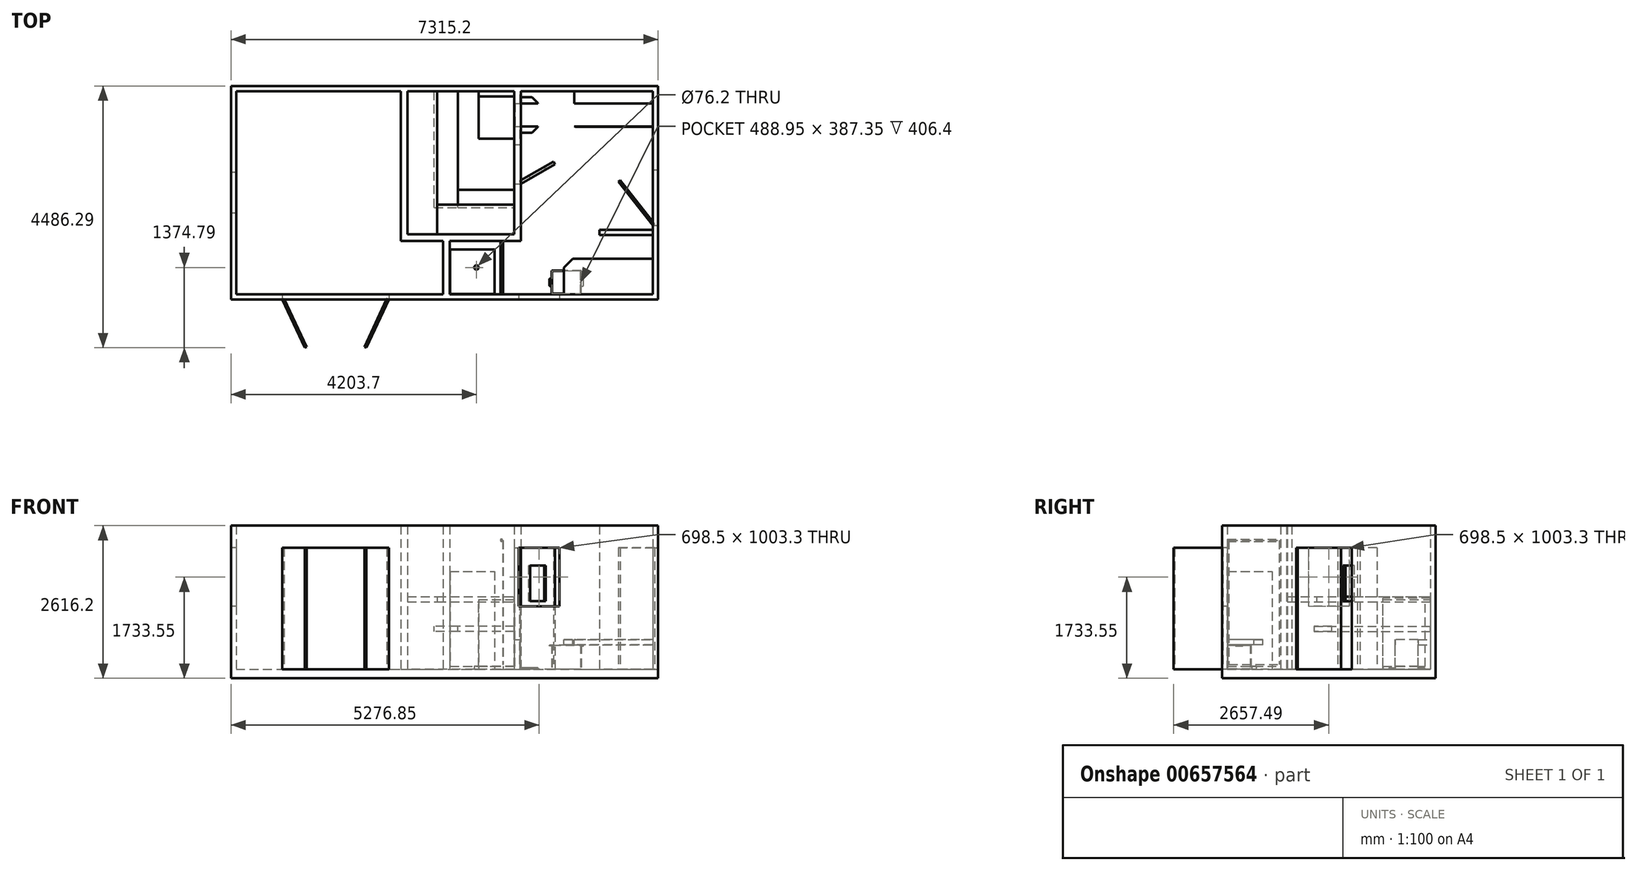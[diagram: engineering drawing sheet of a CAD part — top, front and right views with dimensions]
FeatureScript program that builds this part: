
annotation { "Feature Type Name" : "Feature", "Feature Type Description" : "" }
export const myFeature = defineFeature(function(context is Context, id is Id, definition is map)
    precondition{}
    {
        {
            var Q0;
            Q0=qCreatedBy(makeId("Top.planeOp"),FACE);
            var sketch = newSketch(context, id + "F0", { "sketchPlane" : qUnion([Q0])});
            skLineSegment(sketch, "E0.bottom", {"start": v(-3657.6, -1828.8) * mm, "end": v(3657.6, -1828.8) * mm});
            skLineSegment(sketch, "E0.top", {"start": v(-3657.6, 1828.8) * mm, "end": v(3657.6, 1828.8) * mm});
            skLineSegment(sketch, "E0.left", {"start": v(-3657.6, -1828.8) * mm, "end": v(-3657.6, 1828.8) * mm});
            skLineSegment(sketch, "E0.right", {"start": v(3657.6, -1828.8) * mm, "end": v(3657.6, 1828.8) * mm});
            skPoint(sketch, "E0.middle", {"position": v(0, 0) * mm});
            skSolve(sketch);
        }
        {
            var Q0;
            Q0=makeQuery(id+"F0.imprint","IMPRINT",FACE,{"disambiguationData":[TD([[makeQuery(id+"F0.imprint","IMPRINT",EDGE,{"derivedFrom":sQuery(id+"F0.wireOp",EDGE,"E0.bottom")}),1.0]])]});
            extrude(context, id + "F1", {"entities" : qUnion([Q0]), "depth" : 152.4 * mm});
        }
        {
            var Q0;
            Q0=makeQuery(id+"F1.opExtrude","CAP_FACE",FACE,{"disambiguationData":[OSD([sQuery(id+"F0.wireOp",EDGE,"E0.bottom"),sQuery(id+"F0.wireOp",EDGE,"E0.top"),sQuery(id+"F0.wireOp",EDGE,"E0.left"),sQuery(id+"F0.wireOp",EDGE,"E0.right")])],"isStart":false});
            var sketch = newSketch(context, id + "F2", { "sketchPlane" : qUnion([Q0])});
            skLineSegment(sketch, "E1.0", {"start": v(-3657.6, -1828.8) * mm, "end": v(-3657.6, 1828.8) * mm});
            skLineSegment(sketch, "E1.1", {"start": v(-3657.6, 1828.8) * mm, "end": v(3657.6, 1828.8) * mm});
            skLineSegment(sketch, "E1.2", {"start": v(3657.6, -1828.8) * mm, "end": v(3657.6, 1828.8) * mm});
            skLineSegment(sketch, "E1.3", {"start": v(-3657.6, -1828.8) * mm, "end": v(3657.6, -1828.8) * mm});
            skLineSegment(sketch, "E2.bottom", {"start": v(-3568.7, 1739.9) * mm, "end": v(3568.7, 1739.9) * mm});
            skLineSegment(sketch, "E2.top", {"start": v(-3568.7, -1739.9) * mm, "end": v(3568.7, -1739.9) * mm});
            skLineSegment(sketch, "E2.left", {"start": v(-3568.7, 1739.9) * mm, "end": v(-3568.7, -1739.9) * mm});
            skLineSegment(sketch, "E2.right", {"start": v(3568.7, 1739.9) * mm, "end": v(3568.7, -1739.9) * mm});
            skLineSegment(sketch, "E3", {"start": v(3568.7, 0) * mm, "end": v(0, 0) * mm, "construction": true});
            skSolve(sketch);
        }
        {
            var Q0;
            Q0=qSketchRegion(id+"F2",true);
            extrude(context, id + "F3", {"entities" : qUnion([Q0]), "depth" : 2463.8 * mm});
        }
        {
            var Q0;
            Q0=makeQuery(id+"F3.opExtrude","SWEPT_FACE",FACE,{"disambiguationData":[OSD([sQuery(id+"F2.wireOp",EDGE,"E1.2")])]});
            var sketch = newSketch(context, id + "F4", { "sketchPlane" : qUnion([Q0])});
            skLineSegment(sketch, "E4.bottom", {"start": v(-558.8, 152.4) * mm, "end": v(393.7, 152.4) * mm});
            skLineSegment(sketch, "E4.top", {"start": v(-558.8, 2235.2) * mm, "end": v(393.7, 2235.2) * mm});
            skLineSegment(sketch, "E4.left", {"start": v(-558.8, 152.4) * mm, "end": v(-558.8, 2235.2) * mm});
            skLineSegment(sketch, "E4.right", {"start": v(393.7, 152.4) * mm, "end": v(393.7, 2235.2) * mm});
            skSolve(sketch);
        }
        {
            var Q0;
            Q0=qSketchRegion(id+"F4",true);
            extrude(context, id + "F5", {"entities" : qUnion([Q0]), "operationType" : NewBodyOperationType.REMOVE, "endBound" : BoundingType.UP_TO_NEXT, "oppositeDirection" : true, "depth" : 25.4 * mm});
        }
        {
            var Q0;
            Q0=makeQuery(id+"F3.opExtrude","SWEPT_FACE",FACE,{"disambiguationData":[OSD([sQuery(id+"F2.wireOp",EDGE,"E1.3")])]});
            var sketch = newSketch(context, id + "F6", { "sketchPlane" : qUnion([Q0])});
            skLineSegment(sketch, "E5.bottom", {"start": v(-2781.3, 152.4) * mm, "end": v(-952.5, 152.4) * mm});
            skLineSegment(sketch, "E5.top", {"start": v(-2781.3, 2235.2) * mm, "end": v(-952.5, 2235.2) * mm});
            skLineSegment(sketch, "E5.left", {"start": v(-2781.3, 152.4) * mm, "end": v(-2781.3, 2235.2) * mm});
            skLineSegment(sketch, "E5.right", {"start": v(-952.5, 152.4) * mm, "end": v(-952.5, 2235.2) * mm});
            skLineSegment(sketch, "E6.bottom", {"start": v(1270, 2235.2) * mm, "end": v(1968.5, 2235.2) * mm});
            skLineSegment(sketch, "E6.top", {"start": v(1270, 1231.9) * mm, "end": v(1968.5, 1231.9) * mm});
            skLineSegment(sketch, "E6.left", {"start": v(1270, 2235.2) * mm, "end": v(1270, 1231.9) * mm});
            skLineSegment(sketch, "E6.right", {"start": v(1968.5, 2235.2) * mm, "end": v(1968.5, 1231.9) * mm});
            skSolve(sketch);
        }
        {
            var Q0;
            Q0=qSketchRegion(id+"F6",true);
            extrude(context, id + "F7", {"entities" : qUnion([Q0]), "operationType" : NewBodyOperationType.REMOVE, "endBound" : BoundingType.UP_TO_NEXT, "oppositeDirection" : true, "depth" : 25.4 * mm});
        }
        {
            var Q0;
            Q0=makeQuery(id+"F3.opExtrude","SWEPT_FACE",FACE,{"disambiguationData":[OSD([sQuery(id+"F2.wireOp",EDGE,"E1.0")])]});
            var sketch = newSketch(context, id + "F8", { "sketchPlane" : qUnion([Q0])});
            skLineSegment(sketch, "E7.bottom", {"start": v(-349.25, 2235.2) * mm, "end": v(349.25, 2235.2) * mm});
            skLineSegment(sketch, "E7.top", {"start": v(-349.25, 1231.9) * mm, "end": v(349.25, 1231.9) * mm});
            skLineSegment(sketch, "E7.left", {"start": v(-349.25, 2235.2) * mm, "end": v(-349.25, 1231.9) * mm});
            skLineSegment(sketch, "E7.right", {"start": v(349.25, 2235.2) * mm, "end": v(349.25, 1231.9) * mm});
            skLineSegment(sketch, "E8", {"start": v(0, 2235.2) * mm, "end": v(0, 1231.9) * mm, "construction": true});
            skSolve(sketch);
        }
        {
            var Q0;
            Q0=qSketchRegion(id+"F8",true);
            extrude(context, id + "F9", {"entities" : qUnion([Q0]), "operationType" : NewBodyOperationType.REMOVE, "endBound" : BoundingType.UP_TO_NEXT, "oppositeDirection" : true, "depth" : 25.4 * mm});
        }
        {
            var Q0;
            Q0=makeQuery(id+"F1.opExtrude","CAP_FACE",FACE,{"disambiguationData":[OSD([sQuery(id+"F0.wireOp",EDGE,"E0.bottom"),sQuery(id+"F0.wireOp",EDGE,"E0.top"),sQuery(id+"F0.wireOp",EDGE,"E0.left"),sQuery(id+"F0.wireOp",EDGE,"E0.right")])],"isStart":false});
            var sketch = newSketch(context, id + "F10", { "sketchPlane" : qUnion([Q0])});
            skLineSegment(sketch, "E9.bottom", {"start": v(-25.4, -1739.9) * mm, "end": v(88.9, -1739.9) * mm});
            skLineSegment(sketch, "E9.top", {"start": v(-749.3, 1739.9) * mm, "end": v(-635, 1739.9) * mm});
            skLineSegment(sketch, "E9.left", {"start": v(-25.4, -1739.9) * mm, "end": v(-25.4, -825.5) * mm});
            skLineSegment(sketch, "E9.right", {"start": v(88.9, -1739.9) * mm, "end": v(88.9, -825.5) * mm});
            skLineSegment(sketch, "E10.top", {"start": v(1193.8, 1739.9) * mm, "end": v(1308.1, 1739.9) * mm});
            skLineSegment(sketch, "E11", {"start": v(1193.8, 1739.9) * mm, "end": v(1193.8, -711.2) * mm});
            skLineSegment(sketch, "E12", {"start": v(1193.8, -711.2) * mm, "end": v(-635, -711.2) * mm});
            skLineSegment(sketch, "E13", {"start": v(-749.3, -825.5) * mm, "end": v(1308.1, -825.5) * mm});
            skLineSegment(sketch, "E14", {"start": v(1308.1, -825.5) * mm, "end": v(1308.1, 1739.9) * mm});
            skLineSegment(sketch, "E15", {"start": v(-635, -711.2) * mm, "end": v(-635, 1739.9) * mm});
            skLineSegment(sketch, "E16", {"start": v(-749.3, -825.5) * mm, "end": v(-749.3, 1739.9) * mm});
            skLineSegment(sketch, "E17", {"start": v(-25.4, -825.5) * mm, "end": v(88.9, -825.5) * mm});
            skSolve(sketch);
        }
        {
            var Q0;
            Q0=qSketchRegion(id+"F10",true);
            var Q1;
            Q1=makeQuery(id+"F3.opExtrude","CAP_FACE",FACE,{"disambiguationData":[OSD([sQuery(id+"F2.wireOp",EDGE,"E1.0"),sQuery(id+"F2.wireOp",EDGE,"E1.1"),sQuery(id+"F2.wireOp",EDGE,"E1.2"),sQuery(id+"F2.wireOp",EDGE,"E1.3"),sQuery(id+"F2.wireOp",EDGE,"E2.bottom"),sQuery(id+"F2.wireOp",EDGE,"E2.top"),sQuery(id+"F2.wireOp",EDGE,"E2.left"),sQuery(id+"F2.wireOp",EDGE,"E2.right")])],"isStart":false});
            extrude(context, id + "F11", {"entities" : qUnion([Q0]), "endBound" : BoundingType.UP_TO_SURFACE, "endBoundEntityFace" : qUnion([Q1]), "depth" : 25.4 * mm});
        }
        {
            var Q0;
            Q0=makeQuery(id+"F1.opExtrude","CAP_FACE",FACE,{"disambiguationData":[OSD([sQuery(id+"F0.wireOp",EDGE,"E0.bottom"),sQuery(id+"F0.wireOp",EDGE,"E0.top"),sQuery(id+"F0.wireOp",EDGE,"E0.left"),sQuery(id+"F0.wireOp",EDGE,"E0.right")])],"isStart":false});
            var sketch = newSketch(context, id + "F12", { "sketchPlane" : qUnion([Q0])});
            skLineSegment(sketch, "E18.bottom", {"start": v(3568.7, -723.9) * mm, "end": v(2654.3, -723.9) * mm});
            skLineSegment(sketch, "E18.top", {"start": v(3568.7, -635) * mm, "end": v(2654.3, -635) * mm});
            skLineSegment(sketch, "E18.left", {"start": v(3568.7, -723.9) * mm, "end": v(3568.7, -635) * mm});
            skLineSegment(sketch, "E18.right", {"start": v(2654.3, -723.9) * mm, "end": v(2654.3, -635) * mm});
            skSolve(sketch);
        }
        {
            var Q0;
            Q0=qSketchRegion(id+"F12",true);
            var Q1;
            Q1=makeQuery(id+"F3.opExtrude","CAP_FACE",FACE,{"disambiguationData":[OSD([sQuery(id+"F2.wireOp",EDGE,"E1.0"),sQuery(id+"F2.wireOp",EDGE,"E1.1"),sQuery(id+"F2.wireOp",EDGE,"E1.2"),sQuery(id+"F2.wireOp",EDGE,"E1.3"),sQuery(id+"F2.wireOp",EDGE,"E2.bottom"),sQuery(id+"F2.wireOp",EDGE,"E2.top"),sQuery(id+"F2.wireOp",EDGE,"E2.left"),sQuery(id+"F2.wireOp",EDGE,"E2.right")])],"isStart":false});
            extrude(context, id + "F13", {"entities" : qUnion([Q0]), "endBound" : BoundingType.UP_TO_SURFACE, "endBoundEntityFace" : qUnion([Q1]), "depth" : 25.4 * mm});
        }
        {
            var Q0;
            Q0=makeQuery(id+"F11.opExtrude","SWEPT_FACE",FACE,{"disambiguationData":[OSD([sQuery(id+"F10.wireOp",EDGE,"E14")])]});
            var sketch = newSketch(context, id + "F14", { "sketchPlane" : qUnion([Q0])});
            skLineSegment(sketch, "E19.bottom", {"start": v(152.4, 152.4) * mm, "end": v(825.5, 152.4) * mm});
            skLineSegment(sketch, "E19.top", {"start": v(152.4, 2235.2) * mm, "end": v(825.5, 2235.2) * mm});
            skLineSegment(sketch, "E19.left", {"start": v(152.4, 152.4) * mm, "end": v(152.4, 2235.2) * mm});
            skLineSegment(sketch, "E19.right", {"start": v(825.5, 152.4) * mm, "end": v(825.5, 2235.2) * mm});
            skSolve(sketch);
        }
        {
            var Q0;
            Q0=qSketchRegion(id+"F14",true);
            extrude(context, id + "F15", {"entities" : qUnion([Q0]), "operationType" : NewBodyOperationType.REMOVE, "endBound" : BoundingType.UP_TO_NEXT, "oppositeDirection" : true, "depth" : 25.4 * mm});
        }
        {
            var Q0;
            Q0=qCreatedBy(makeId("Front.planeOp"),FACE);
            var sketch = newSketch(context, id + "F16", { "sketchPlane" : qUnion([Q0])});
            skLineSegment(sketch, "E20.bottom", {"start": v(88.9, 152.4) * mm, "end": v(127, 152.4) * mm});
            skLineSegment(sketch, "E20.top", {"start": v(88.9, 1397) * mm, "end": v(127, 1397) * mm});
            skLineSegment(sketch, "E20.left", {"start": v(88.9, 152.4) * mm, "end": v(88.9, 1397) * mm});
            skLineSegment(sketch, "E20.right", {"start": v(127, 152.4) * mm, "end": v(127, 1397) * mm});
            skSolve(sketch);
        }
        {
            var Q0;
            Q0=qSketchRegion(id+"F16",true);
            extrude(context, id + "F17", {"entities" : qUnion([Q0]), "endBound" : BoundingType.SYMMETRIC, "depth" : 88.9 * mm});
        }
        {
            var Q0;
            Q0=makeQuery(id+"F17.opExtrude","SWEPT_BODY",BODY,{"disambiguationData":[OSD([sQuery(id+"F16.wireOp",EDGE,"E20.bottom"),sQuery(id+"F16.wireOp",EDGE,"E20.top"),sQuery(id+"F16.wireOp",EDGE,"E20.left"),sQuery(id+"F16.wireOp",EDGE,"E20.right")])]});
            deleteBodies(context, id + "F18", {"entities" : qUnion([Q0])});
        }
        {
            var Q0;
            Q0=qCreatedBy(makeId("Front.planeOp"),FACE);
            var sketch = newSketch(context, id + "F19", { "sketchPlane" : qUnion([Q0])});
            skLineSegment(sketch, "E21.bottom", {"start": v(-635, 1397) * mm, "end": v(-127, 1397) * mm});
            skLineSegment(sketch, "E21.top", {"start": v(-635, 1308.1) * mm, "end": v(-127, 1308.1) * mm});
            skLineSegment(sketch, "E21.left", {"start": v(-635, 1397) * mm, "end": v(-635, 1308.1) * mm});
            skLineSegment(sketch, "E21.right", {"start": v(-127, 1397) * mm, "end": v(-127, 1308.1) * mm});
            skSolve(sketch);
        }
        {
            var Q0;
            Q0=qSketchRegion(id+"F19",true);
            extrude(context, id + "F20", {"entities" : qUnion([Q0]), "endBound" : BoundingType.UP_TO_NEXT, "depth" : 812.8 * mm, "hasSecondDirection" : true, "secondDirectionBound" : SecondDirectionBoundingType.UP_TO_NEXT, "secondDirectionOppositeDirection" : true, "secondDirectionDepth" : 25.4 * mm, "offsetDistance" : 25.4 * mm});
        }
        {
            var Q0;
            Q0=makeQuery(id+"F20.opExtrude","SWEPT_FACE",FACE,{"disambiguationData":[OSD([sQuery(id+"F19.wireOp",EDGE,"E21.bottom")])]});
            var sketch = newSketch(context, id + "F21", { "sketchPlane" : qUnion([Q0])});
            skLineSegment(sketch, "E22.top", {"start": v(-127, -711.2) * mm, "end": v(1193.8, -711.2) * mm});
            skLineSegment(sketch, "E22.left", {"start": v(-127, -711.2) * mm, "end": v(-127, -203.2) * mm});
            skLineSegment(sketch, "E22.right", {"start": v(1193.8, -711.2) * mm, "end": v(1193.8, -203.2) * mm});
            skLineSegment(sketch, "E23", {"start": v(1193.8, -203.2) * mm, "end": v(-127, -203.2) * mm});
            skSolve(sketch);
        }
        {
            var Q0;
            Q0=qSketchRegion(id+"F21",true);
            var Q1;
            Q1=makeQuery(id+"F20.opExtrude","CAP_VERTEX",VERTEX,{"disambiguationData":[OSD([sQuery(id+"F2.wireOp",EDGE,"E2.top"),sQuery(id+"F19.wireOp",EDGE,"E21.top"),sQuery(id+"F19.wireOp",EDGE,"E21.right")])],"isStart":false});
            extrude(context, id + "F22", {"entities" : qUnion([Q0]), "endBound" : BoundingType.UP_TO_VERTEX, "oppositeDirection" : true, "endBoundEntityVertex" : qUnion([Q1]), "depth" : 25.4 * mm});
        }
        {
            var Q0;
            Q0=qCreatedBy(makeId("Front.planeOp"),FACE);
            var sketch = newSketch(context, id + "F23", { "sketchPlane" : qUnion([Q0])});
            skLineSegment(sketch, "E24.bottom", {"start": v(-177.8, 889) * mm, "end": v(228.6, 889) * mm});
            skLineSegment(sketch, "E24.top", {"start": v(-177.8, 800.1) * mm, "end": v(228.6, 800.1) * mm});
            skLineSegment(sketch, "E24.left", {"start": v(-177.8, 889) * mm, "end": v(-177.8, 800.1) * mm});
            skLineSegment(sketch, "E24.right", {"start": v(228.6, 889) * mm, "end": v(228.6, 800.1) * mm});
            skSolve(sketch);
        }
        {
            var Q0;
            Q0=qSketchRegion(id+"F23",true);
            extrude(context, id + "F24", {"entities" : qUnion([Q0]), "depth" : 254 * mm, "hasSecondDirection" : true, "secondDirectionBound" : SecondDirectionBoundingType.UP_TO_NEXT, "secondDirectionOppositeDirection" : true, "secondDirectionDepth" : 1282.7 * mm, "offsetDistance" : 25.4 * mm});
        }
        {
            var Q0;
            Q0=makeQuery(id+"F24.opExtrude","SWEPT_FACE",FACE,{"disambiguationData":[OSD([sQuery(id+"F23.wireOp",EDGE,"E24.bottom")])]});
            var sketch = newSketch(context, id + "F25", { "sketchPlane" : qUnion([Q0])});
            skLineSegment(sketch, "E25.bottom", {"start": v(1193.8, 50.8) * mm, "end": v(228.6, 50.8) * mm});
            skLineSegment(sketch, "E25.top", {"start": v(228.6, -254) * mm, "end": v(1193.8, -254) * mm});
            skLineSegment(sketch, "E25.left", {"start": v(228.6, 50.8) * mm, "end": v(228.6, -254) * mm});
            skLineSegment(sketch, "E25.right", {"start": v(1193.8, 50.8) * mm, "end": v(1193.8, -254) * mm});
            skSolve(sketch);
        }
        {
            var Q0;
            Q0=makeQuery(id+"F3.opExtrude","SWEPT_FACE",FACE,{"disambiguationData":[OSD([sQuery(id+"F2.wireOp",EDGE,"E2.bottom")])]});
            var sketch = newSketch(context, id + "F26", { "sketchPlane" : qUnion([Q0])});
            skLineSegment(sketch, "E26.bottom", {"start": v(3568.7, 660.4) * mm, "end": v(2222.5, 660.4) * mm});
            skLineSegment(sketch, "E26.top", {"start": v(2222.5, 571.5) * mm, "end": v(3568.7, 571.5) * mm});
            skLineSegment(sketch, "E26.left", {"start": v(3568.7, 660.4) * mm, "end": v(3568.7, 571.5) * mm});
            skLineSegment(sketch, "E26.right", {"start": v(2222.5, 660.4) * mm, "end": v(2222.5, 571.5) * mm});
            skSolve(sketch);
        }
        {
            var Q0;
            Q0=qSketchRegion(id+"F26",true);
            extrude(context, id + "F27", {"entities" : qUnion([Q0]), "depth" : 609.6 * mm});
        }
        {
            var Q0;
            Q0=makeQuery(id+"F27.opExtrude","SWEPT_FACE",FACE,{"disambiguationData":[OSD([sQuery(id+"F26.wireOp",EDGE,"E26.bottom")])]});
            var sketch = newSketch(context, id + "F28", { "sketchPlane" : qUnion([Q0])});
            skLineSegment(sketch, "E27.bottom", {"start": v(2222.5, 1130.3) * mm, "end": v(2628.9, 1130.3) * mm});
            skLineSegment(sketch, "E27.top", {"start": v(2222.5, 114.3) * mm, "end": v(2628.9, 114.3) * mm});
            skLineSegment(sketch, "E27.left", {"start": v(2222.5, 114.3) * mm, "end": v(2222.5, 1130.3) * mm});
            skLineSegment(sketch, "E27.right", {"start": v(2628.9, 114.3) * mm, "end": v(2628.9, 1130.3) * mm});
            skSolve(sketch);
        }
        {
            var Q0;
            Q0=qSketchRegion(id+"F25",true);
            var Q1;
            Q1=makeQuery(id+"F24.opExtrude","CAP_VERTEX",VERTEX,{"disambiguationData":[OSD([sQuery(id+"F23.wireOp",EDGE,"E24.top"),sQuery(id+"F23.wireOp",EDGE,"E24.right")])],"isStart":true});
            extrude(context, id + "F29", {"entities" : qUnion([Q0]), "endBound" : BoundingType.UP_TO_VERTEX, "oppositeDirection" : true, "endBoundEntityVertex" : qUnion([Q1]), "depth" : 25.4 * mm});
        }
        {
            var Q0;
            Q0=makeQuery(id+"F1.opExtrude","CAP_FACE",FACE,{"disambiguationData":[OSD([sQuery(id+"F0.wireOp",EDGE,"E0.bottom"),sQuery(id+"F0.wireOp",EDGE,"E0.top"),sQuery(id+"F0.wireOp",EDGE,"E0.left"),sQuery(id+"F0.wireOp",EDGE,"E0.right")])],"isStart":false});
            var sketch = newSketch(context, id + "F30", { "sketchPlane" : qUnion([Q0])});
            skLineSegment(sketch, "E28", {"start": v(1282.7, 196.4) * mm, "end": v(1308.1, 152.4) * mm});
            skLineSegment(sketch, "E29", {"start": v(1308.1, 152.4) * mm, "end": v(1891.02, 488.95) * mm});
            skLineSegment(sketch, "E30", {"start": v(1891.02, 488.95) * mm, "end": v(1865.62, 532.94) * mm});
            skLineSegment(sketch, "E31", {"start": v(1865.62, 532.94) * mm, "end": v(1282.7, 196.4) * mm});
            skSolve(sketch);
        }
        {
            var Q0;
            Q0=qSketchRegion(id+"F30",true);
            extrude(context, id + "F31", {"entities" : qUnion([Q0]), "depth" : 2082.8 * mm});
        }
        {
            var Q0;
            Q0=makeQuery(id+"F1.opExtrude","CAP_FACE",FACE,{"disambiguationData":[OSD([sQuery(id+"F0.wireOp",EDGE,"E0.bottom"),sQuery(id+"F0.wireOp",EDGE,"E0.top"),sQuery(id+"F0.wireOp",EDGE,"E0.left"),sQuery(id+"F0.wireOp",EDGE,"E0.right")])],"isStart":false});
            var sketch = newSketch(context, id + "F32", { "sketchPlane" : qUnion([Q0])});
            skLineSegment(sketch, "E32", {"start": v(3568.7, -558.8) * mm, "end": v(3598.59, -535.17) * mm});
            skLineSegment(sketch, "E33", {"start": v(3598.59, -535.17) * mm, "end": v(3007.81, 211.99) * mm});
            skLineSegment(sketch, "E34", {"start": v(3007.81, 211.99) * mm, "end": v(2977.93, 188.36) * mm});
            skLineSegment(sketch, "E35", {"start": v(2977.93, 188.36) * mm, "end": v(3568.7, -558.8) * mm});
            skSolve(sketch);
        }
        {
            var Q0;
            Q0=qSketchRegion(id+"F32",true);
            extrude(context, id + "F33", {"entities" : qUnion([Q0]), "depth" : 2082.8 * mm});
        }
        {
            var Q0;
            Q0=makeQuery(id+"F1.opExtrude","CAP_FACE",FACE,{"disambiguationData":[OSD([sQuery(id+"F0.wireOp",EDGE,"E0.bottom"),sQuery(id+"F0.wireOp",EDGE,"E0.top"),sQuery(id+"F0.wireOp",EDGE,"E0.left"),sQuery(id+"F0.wireOp",EDGE,"E0.right")])],"isStart":false});
            var sketch = newSketch(context, id + "F34", { "sketchPlane" : qUnion([Q0])});
            skLineSegment(sketch, "E36", {"start": v(88.9, -1739.9) * mm, "end": v(88.9, -971.55) * mm});
            skLineSegment(sketch, "E37", {"start": v(88.9, -1739.9) * mm, "end": v(857.25, -1739.9) * mm});
            skLineSegment(sketch, "E38.0", {"start": v(95.25, -1733.55) * mm, "end": v(857.25, -1733.55) * mm});
            skLineSegment(sketch, "E38.1", {"start": v(95.25, -1733.55) * mm, "end": v(95.25, -971.55) * mm});
            skLineSegment(sketch, "E39", {"start": v(88.9, -971.55) * mm, "end": v(95.25, -971.55) * mm});
            skLineSegment(sketch, "E40", {"start": v(857.25, -1739.9) * mm, "end": v(857.25, -1733.55) * mm});
            skSolve(sketch);
        }
        {
            var Q0;
            Q0=qSketchRegion(id+"F34",true);
            extrude(context, id + "F35", {"entities" : qUnion([Q0]), "depth" : 1676.4 * mm});
        }
        {
            var Q0;
            Q0=makeQuery(id+"F1.opExtrude","CAP_FACE",FACE,{"disambiguationData":[OSD([sQuery(id+"F0.wireOp",EDGE,"E0.bottom"),sQuery(id+"F0.wireOp",EDGE,"E0.top"),sQuery(id+"F0.wireOp",EDGE,"E0.left"),sQuery(id+"F0.wireOp",EDGE,"E0.right")])],"isStart":false});
            var sketch = newSketch(context, id + "F36", { "sketchPlane" : qUnion([Q0])});
            skLineSegment(sketch, "E41.bottom", {"start": v(88.9, -1739.9) * mm, "end": v(857.25, -1739.9) * mm});
            skLineSegment(sketch, "E41.top", {"start": v(88.9, -971.55) * mm, "end": v(857.25, -971.55) * mm});
            skLineSegment(sketch, "E41.left", {"start": v(88.9, -1739.9) * mm, "end": v(88.9, -971.55) * mm});
            skLineSegment(sketch, "E41.right", {"start": v(857.25, -1739.9) * mm, "end": v(857.25, -971.55) * mm});
            skSolve(sketch);
        }
        {
            var Q0;
            Q0=qSketchRegion(id+"F36",true);
            extrude(context, id + "F37", {"entities" : qUnion([Q0]), "operationType" : NewBodyOperationType.ADD, "depth" : 50.8 * mm});
        }
        {
            var Q0;
            Q0=makeQuery(id+"F1.opExtrude","CAP_FACE",FACE,{"disambiguationData":[OSD([sQuery(id+"F0.wireOp",EDGE,"E0.bottom"),sQuery(id+"F0.wireOp",EDGE,"E0.top"),sQuery(id+"F0.wireOp",EDGE,"E0.left"),sQuery(id+"F0.wireOp",EDGE,"E0.right")])],"isStart":false});
            var sketch = newSketch(context, id + "F38", { "sketchPlane" : qUnion([Q0])});
            skLineSegment(sketch, "E42.bottom", {"start": v(88.9, -1739.9) * mm, "end": v(1003.3, -1739.9) * mm});
            skLineSegment(sketch, "E42.top", {"start": v(88.9, -825.5) * mm, "end": v(1003.3, -825.5) * mm});
            skLineSegment(sketch, "E42.left", {"start": v(88.9, -1739.9) * mm, "end": v(88.9, -825.5) * mm});
            skLineSegment(sketch, "E42.right", {"start": v(1003.3, -1739.9) * mm, "end": v(1003.3, -825.5) * mm});
            skCircle(sketch, "E43", {"center": v(546.1, -1282.7) * mm, "radius": 38.1 * mm});
            skLineSegment(sketch, "E44", {"start": v(546.1, -825.5) * mm, "end": v(546.1, -1739.9) * mm, "construction": true});
            skSolve(sketch);
        }
        {
            var Q0;
            Q0=qSketchRegion(id+"F38",true);
            extrude(context, id + "F39", {"entities" : qUnion([Q0]), "depth" : 50.8 * mm});
        }
        {
            var Q0;
            Q0=makeQuery(id+"F3.opExtrude","SWEPT_FACE",FACE,{"disambiguationData":[OSD([sQuery(id+"F2.wireOp",EDGE,"E2.top")])]});
            var sketch = newSketch(context, id + "F40", { "sketchPlane" : qUnion([Q0])});
            skLineSegment(sketch, "E45.bottom", {"start": v(-3568.7, 660.4) * mm, "end": v(-2044.7, 660.4) * mm});
            skLineSegment(sketch, "E45.top", {"start": v(-3568.7, 571.5) * mm, "end": v(-2044.7, 571.5) * mm});
            skLineSegment(sketch, "E45.left", {"start": v(-3568.7, 660.4) * mm, "end": v(-3568.7, 571.5) * mm});
            skLineSegment(sketch, "E45.right", {"start": v(-2044.7, 660.4) * mm, "end": v(-2044.7, 571.5) * mm});
            skSolve(sketch);
        }
        {
            var Q0;
            Q0=qSketchRegion(id+"F40",true);
            extrude(context, id + "F41", {"entities" : qUnion([Q0]), "depth" : 609.6 * mm});
        }
        {
            var Q0;
            Q0=makeQuery(id+"F41.opExtrude","SWEPT_FACE",FACE,{"disambiguationData":[OSD([sQuery(id+"F40.wireOp",EDGE,"E45.bottom")])]});
            var sketch = newSketch(context, id + "F42", { "sketchPlane" : qUnion([Q0])});
            skLineSegment(sketch, "E46", {"start": v(2044.7, -1130.3) * mm, "end": v(2044.7, -1282.7) * mm});
            skLineSegment(sketch, "E47", {"start": v(2044.7, -1282.7) * mm, "end": v(2197.1, -1130.3) * mm});
            skLineSegment(sketch, "E48", {"start": v(2197.1, -1130.3) * mm, "end": v(2044.7, -1130.3) * mm});
            skSolve(sketch);
        }
        {
            var Q0;
            Q0=qSketchRegion(id+"F42",true);
            extrude(context, id + "F43", {"entities" : qUnion([Q0]), "operationType" : NewBodyOperationType.REMOVE, "endBound" : BoundingType.UP_TO_NEXT, "oppositeDirection" : true, "depth" : 25.4 * mm});
        }
        {
            var Q0;
            Q0=makeQuery(id+"F31.opExtrude","SWEPT_FACE",FACE,{"disambiguationData":[OSD([sQuery(id+"F30.wireOp",EDGE,"E29")])]});
            var sketch = newSketch(context, id + "F44", { "sketchPlane" : qUnion([Q0])});
            skLineSegment(sketch, "E49.bottom", {"start": v(1393.2, 1930.4) * mm, "end": v(1698, 1930.4) * mm});
            skLineSegment(sketch, "E49.top", {"start": v(1393.2, 1320.8) * mm, "end": v(1698, 1320.8) * mm});
            skLineSegment(sketch, "E49.left", {"start": v(1393.2, 1930.4) * mm, "end": v(1393.2, 1320.8) * mm});
            skLineSegment(sketch, "E49.right", {"start": v(1698, 1930.4) * mm, "end": v(1698, 1320.8) * mm});
            skLineSegment(sketch, "E50", {"start": v(1545.6, 2235.2) * mm, "end": v(1545.6, 1930.4) * mm, "construction": true});
            skSolve(sketch);
        }
        {
            var Q0;
            Q0=qSketchRegion(id+"F44",true);
            extrude(context, id + "F45", {"entities" : qUnion([Q0]), "operationType" : NewBodyOperationType.REMOVE, "endBound" : BoundingType.UP_TO_NEXT, "oppositeDirection" : true, "depth" : 25.4 * mm});
        }
        {
            var Q0;
            Q0=makeQuery(id+"F1.opExtrude","CAP_FACE",FACE,{"disambiguationData":[OSD([sQuery(id+"F0.wireOp",EDGE,"E0.bottom"),sQuery(id+"F0.wireOp",EDGE,"E0.top"),sQuery(id+"F0.wireOp",EDGE,"E0.left"),sQuery(id+"F0.wireOp",EDGE,"E0.right")])],"isStart":false});
            var sketch = newSketch(context, id + "F46", { "sketchPlane" : qUnion([Q0])});
            skLineSegment(sketch, "E51", {"start": v(1193.8, 927.1) * mm, "end": v(584.2, 927.1) * mm});
            skLineSegment(sketch, "E52", {"start": v(584.2, 927.1) * mm, "end": v(584.2, 1739.9) * mm});
            skLineSegment(sketch, "E53", {"start": v(584.2, 1739.9) * mm, "end": v(1193.8, 1739.9) * mm});
            skLineSegment(sketch, "E54", {"start": v(1193.8, 1739.9) * mm, "end": v(1193.8, 1530.35) * mm});
            skLineSegment(sketch, "E55", {"start": v(1193.8, 1136.65) * mm, "end": v(1295.4, 1136.65) * mm});
            skLineSegment(sketch, "E56", {"start": v(1295.4, 1136.65) * mm, "end": v(1295.4, 1530.35) * mm});
            skLineSegment(sketch, "E57", {"start": v(1295.4, 1530.35) * mm, "end": v(1193.8, 1530.35) * mm});
            skLineSegment(sketch, "E58.trimOffspring", {"start": v(1193.8, 1136.65) * mm, "end": v(1193.8, 927.1) * mm});
            skSolve(sketch);
        }
        {
            var Q0;
            Q0=qSketchRegion(id+"F46",true);
            extrude(context, id + "F47", {"entities" : qUnion([Q0]), "depth" : 50.8 * mm});
        }
        {
            var Q0;
            Q0=makeQuery(id+"F1.opExtrude","CAP_FACE",FACE,{"disambiguationData":[OSD([sQuery(id+"F0.wireOp",EDGE,"E0.bottom"),sQuery(id+"F0.wireOp",EDGE,"E0.top"),sQuery(id+"F0.wireOp",EDGE,"E0.left"),sQuery(id+"F0.wireOp",EDGE,"E0.right")])],"isStart":false});
            var sketch = newSketch(context, id + "F48", { "sketchPlane" : qUnion([Q0])});
            skLineSegment(sketch, "E59", {"start": v(1295.4, 1028.7) * mm, "end": v(1498.6, 1028.7) * mm});
            skLineSegment(sketch, "E60", {"start": v(1498.6, 1028.7) * mm, "end": v(1600.2, 1130.3) * mm});
            skLineSegment(sketch, "E61", {"start": v(1600.2, 1130.3) * mm, "end": v(1600.2, 1536.7) * mm});
            skLineSegment(sketch, "E62", {"start": v(1600.2, 1536.7) * mm, "end": v(1498.6, 1638.3) * mm});
            skLineSegment(sketch, "E63", {"start": v(1498.6, 1638.3) * mm, "end": v(1295.4, 1638.3) * mm});
            skLineSegment(sketch, "E64", {"start": v(1295.4, 1638.3) * mm, "end": v(1295.4, 1028.7) * mm});
            skLineSegment(sketch, "E65", {"start": v(1295.4, 1333.5) * mm, "end": v(1600.2, 1333.5) * mm, "construction": true});
            skSolve(sketch);
        }
        {
            var Q0;
            Q0=qSketchRegion(id+"F48",true);
            extrude(context, id + "F49", {"entities" : qUnion([Q0]), "depth" : 25.4 * mm});
        }
        {
            var Q0;
            Q0=makeQuery(id+"F11.opExtrude","SWEPT_FACE",FACE,{"disambiguationData":[OSD([sQuery(id+"F10.wireOp",EDGE,"E13")])]});
            var sketch = newSketch(context, id + "F50", { "sketchPlane" : qUnion([Q0])});
            skCircle(sketch, "E66", {"center": v(975.9, 2367.47) * mm, "radius": 19.05 * mm});
            skSolve(sketch);
        }
        {
            var Q0;
            Q0=qSketchRegion(id+"F50",true);
            extrude(context, id + "F51", {"entities" : qUnion([Q0]), "endBound" : BoundingType.UP_TO_NEXT, "depth" : 25.4 * mm, "offsetDistance" : 25.4 * mm});
        }
        {
            var Q0;
            Q0=makeQuery(id+"F39.opExtrude","SWEPT_FACE",FACE,{"disambiguationData":[OSD([sQuery(id+"F38.wireOp",EDGE,"E42.right")])]});
            var sketch = newSketch(context, id + "F52", { "sketchPlane" : qUnion([Q0])});
            skLineSegment(sketch, "E67.bottom", {"start": v(-1714.5, 2363.56) * mm, "end": v(-850.9, 2363.56) * mm});
            skLineSegment(sketch, "E67.top", {"start": v(-1714.5, 238.7) * mm, "end": v(-850.9, 238.7) * mm});
            skLineSegment(sketch, "E67.left", {"start": v(-1714.5, 2363.56) * mm, "end": v(-1714.5, 238.7) * mm});
            skLineSegment(sketch, "E67.right", {"start": v(-850.9, 2363.56) * mm, "end": v(-850.9, 238.7) * mm});
            skSolve(sketch);
        }
        {
            var Q0;
            Q0=qSketchRegion(id+"F52",true);
            extrude(context, id + "F53", {"entities" : qUnion([Q0]), "oppositeDirection" : true, "depth" : 3.17 * mm});
        }
        {
            var Q0;
            Q0=makeQuery(id+"F1.opExtrude","CAP_FACE",FACE,{"disambiguationData":[OSD([sQuery(id+"F0.wireOp",EDGE,"E0.bottom"),sQuery(id+"F0.wireOp",EDGE,"E0.top"),sQuery(id+"F0.wireOp",EDGE,"E0.left"),sQuery(id+"F0.wireOp",EDGE,"E0.right")])],"isStart":false});
            var sketch = newSketch(context, id + "F54", { "sketchPlane" : qUnion([Q0])});
            skLineSegment(sketch, "E68.bottom", {"start": v(2343, -1739.9) * mm, "end": v(1835, -1739.9) * mm});
            skLineSegment(sketch, "E68.top", {"start": v(2343, -1333.5) * mm, "end": v(1835, -1333.5) * mm});
            skLineSegment(sketch, "E68.left", {"start": v(2343, -1739.9) * mm, "end": v(2343, -1333.5) * mm});
            skLineSegment(sketch, "E68.right", {"start": v(1835, -1739.9) * mm, "end": v(1835, -1333.5) * mm});
            skSolve(sketch);
        }
        {
            var Q0;
            Q0=qSketchRegion(id+"F54",true);
            extrude(context, id + "F55", {"entities" : qUnion([Q0]), "depth" : 9.52 * mm});
        }
        {
            var Q0;
            Q0=makeQuery(id+"F55.opExtrude","CAP_FACE",FACE,{"disambiguationData":[OSD([sQuery(id+"F54.wireOp",EDGE,"E68.bottom"),sQuery(id+"F54.wireOp",EDGE,"E68.top"),sQuery(id+"F54.wireOp",EDGE,"E68.left"),sQuery(id+"F54.wireOp",EDGE,"E68.right")])],"isStart":false});
            var sketch = newSketch(context, id + "F56", { "sketchPlane" : qUnion([Q0])});
            skLineSegment(sketch, "E69", {"start": v(2343, -1739.9) * mm, "end": v(2343, -1333.5) * mm});
            skLineSegment(sketch, "E70", {"start": v(2343, -1333.5) * mm, "end": v(1835, -1333.5) * mm});
            skLineSegment(sketch, "E71", {"start": v(1835, -1333.5) * mm, "end": v(1835, -1739.9) * mm});
            skLineSegment(sketch, "E72", {"start": v(1835, -1739.9) * mm, "end": v(2343, -1739.9) * mm});
            skLineSegment(sketch, "E73.0", {"start": v(1844.52, -1730.38) * mm, "end": v(2333.47, -1730.38) * mm});
            skLineSegment(sketch, "E73.1", {"start": v(1844.52, -1343.02) * mm, "end": v(1844.52, -1730.38) * mm});
            skLineSegment(sketch, "E73.2", {"start": v(2333.47, -1343.02) * mm, "end": v(1844.52, -1343.02) * mm});
            skLineSegment(sketch, "E73.3", {"start": v(2333.47, -1730.38) * mm, "end": v(2333.47, -1343.02) * mm});
            skSolve(sketch);
        }
        {
            var Q0;
            Q0=qSketchRegion(id+"F56",true);
            extrude(context, id + "F57", {"entities" : qUnion([Q0]), "operationType" : NewBodyOperationType.ADD, "depth" : 406.4 * mm});
        }
        {
            var Q0;
            Q0=makeQuery(id+"F57.opExtrude","CAP_FACE",FACE,{"disambiguationData":[OSD([sQuery(id+"F56.wireOp",EDGE,"E69"),sQuery(id+"F56.wireOp",EDGE,"E70"),sQuery(id+"F56.wireOp",EDGE,"E71"),sQuery(id+"F56.wireOp",EDGE,"E72"),sQuery(id+"F56.wireOp",EDGE,"E73.0"),sQuery(id+"F56.wireOp",EDGE,"E73.1"),sQuery(id+"F56.wireOp",EDGE,"E73.2"),sQuery(id+"F56.wireOp",EDGE,"E73.3")])],"isStart":false});
            var sketch = newSketch(context, id + "F58", { "sketchPlane" : qUnion([Q0])});
            skLineSegment(sketch, "E74.bottom", {"start": v(1835, -1600.2) * mm, "end": v(1809.6, -1600.2) * mm});
            skLineSegment(sketch, "E74.top", {"start": v(1835, -1473.2) * mm, "end": v(1809.6, -1473.2) * mm});
            skLineSegment(sketch, "E74.left", {"start": v(1835, -1600.2) * mm, "end": v(1835, -1473.2) * mm});
            skLineSegment(sketch, "E74.right", {"start": v(1796.9, -1587.5) * mm, "end": v(1796.9, -1485.9) * mm});
            skLineSegment(sketch, "E75.bottom", {"start": v(2343, -1600.2) * mm, "end": v(2368.4, -1600.2) * mm});
            skLineSegment(sketch, "E75.top", {"start": v(2343, -1473.2) * mm, "end": v(2368.4, -1473.2) * mm});
            skLineSegment(sketch, "E75.left", {"start": v(2343, -1600.2) * mm, "end": v(2343, -1473.2) * mm});
            skLineSegment(sketch, "E75.right", {"start": v(2381.1, -1587.5) * mm, "end": v(2381.1, -1485.9) * mm});
            skPoint(sketch, "E76.visualSharp", {"position": v(2381.1, -1600.2) * mm});
            skArc(sketch, "E76.filletArc", {"start": v(2368.4, -1600.2) * mm, "mid": v(2377.38, -1596.48) * mm, "end": v(2381.1, -1587.5) * mm});
            skPoint(sketch, "E77.visualSharp", {"position": v(2381.1, -1473.2) * mm});
            skArc(sketch, "E77.filletArc", {"start": v(2381.1, -1485.9) * mm, "mid": v(2377.38, -1476.92) * mm, "end": v(2368.4, -1473.2) * mm});
            skPoint(sketch, "E78.visualSharp", {"position": v(1796.9, -1600.2) * mm});
            skArc(sketch, "E78.filletArc", {"start": v(1796.9, -1587.5) * mm, "mid": v(1800.62, -1596.48) * mm, "end": v(1809.6, -1600.2) * mm});
            skPoint(sketch, "E79.visualSharp", {"position": v(1796.9, -1473.2) * mm});
            skArc(sketch, "E79.filletArc", {"start": v(1809.6, -1473.2) * mm, "mid": v(1800.62, -1476.92) * mm, "end": v(1796.9, -1485.9) * mm});
            skPoint(sketch, "E80", {"position": v(2333.47, -1536.7) * mm});
            skLineSegment(sketch, "E81", {"start": v(2343, -1536.7) * mm, "end": v(1835, -1536.7) * mm, "construction": true});
            skSolve(sketch);
        }
        {
            var Q0;
            Q0=qSketchRegion(id+"F58",true);
            extrude(context, id + "F59", {"entities" : qUnion([Q0]), "operationType" : NewBodyOperationType.ADD, "oppositeDirection" : true, "depth" : 12.7 * mm});
        }
        {
            var Q0;
            Q0=makeQuery(id+"F1.opExtrude","CAP_FACE",FACE,{"disambiguationData":[OSD([sQuery(id+"F0.wireOp",EDGE,"E0.bottom"),sQuery(id+"F0.wireOp",EDGE,"E0.top"),sQuery(id+"F0.wireOp",EDGE,"E0.left"),sQuery(id+"F0.wireOp",EDGE,"E0.right")])],"isStart":false});
            var sketch = newSketch(context, id + "F60", { "sketchPlane" : qUnion([Q0])});
            skLineSegment(sketch, "E82.bottom", {"start": v(3657.6, -1828.8) * mm, "end": v(3619.5, -1828.8) * mm});
            skLineSegment(sketch, "E82.top", {"start": v(3657.6, 1828.8) * mm, "end": v(3619.5, 1828.8) * mm});
            skLineSegment(sketch, "E82.left", {"start": v(3657.6, -1828.8) * mm, "end": v(3657.6, 1828.8) * mm});
            skLineSegment(sketch, "E82.right", {"start": v(3619.5, -1828.8) * mm, "end": v(3619.5, 1828.8) * mm});
            skLineSegment(sketch, "E83.1.0.0", {"start": v(3213.1, -1828.8) * mm, "end": v(3213.1, 1828.8) * mm});
            skLineSegment(sketch, "E83.1.0.1", {"start": v(3251.2, -1828.8) * mm, "end": v(3251.2, 1828.8) * mm});
            skLineSegment(sketch, "E83.2.0.0", {"start": v(2806.7, -1828.8) * mm, "end": v(2806.7, 1828.8) * mm});
            skLineSegment(sketch, "E83.2.0.1", {"start": v(2844.8, -1828.8) * mm, "end": v(2844.8, 1828.8) * mm});
            skLineSegment(sketch, "E83.3.0.0", {"start": v(2400.3, -1828.8) * mm, "end": v(2400.3, 1828.8) * mm});
            skLineSegment(sketch, "E83.3.0.1", {"start": v(2438.4, -1828.8) * mm, "end": v(2438.4, 1828.8) * mm});
            skLineSegment(sketch, "E83.4.0.0", {"start": v(1993.9, -1828.8) * mm, "end": v(1993.9, 1828.8) * mm});
            skLineSegment(sketch, "E83.4.0.1", {"start": v(2032, -1828.8) * mm, "end": v(2032, 1828.8) * mm});
            skLineSegment(sketch, "E83.5.0.0", {"start": v(1587.5, -1828.8) * mm, "end": v(1587.5, 1828.8) * mm});
            skLineSegment(sketch, "E83.5.0.1", {"start": v(1625.6, -1828.8) * mm, "end": v(1625.6, 1828.8) * mm});
            skLineSegment(sketch, "E83.6.0.0", {"start": v(1181.1, -1828.8) * mm, "end": v(1181.1, 1828.8) * mm});
            skLineSegment(sketch, "E83.6.0.1", {"start": v(1219.2, -1828.8) * mm, "end": v(1219.2, 1828.8) * mm});
            skLineSegment(sketch, "E83.7.0.0", {"start": v(774.7, -1828.8) * mm, "end": v(774.7, 1828.8) * mm});
            skLineSegment(sketch, "E83.7.0.1", {"start": v(812.8, -1828.8) * mm, "end": v(812.8, 1828.8) * mm});
            skLineSegment(sketch, "E83.8.0.0", {"start": v(368.3, -1828.8) * mm, "end": v(368.3, 1828.8) * mm});
            skLineSegment(sketch, "E83.8.0.1", {"start": v(406.4, -1828.8) * mm, "end": v(406.4, 1828.8) * mm});
            skLineSegment(sketch, "E83.9.0.0", {"start": v(-38.1, -1828.8) * mm, "end": v(-38.1, 1828.8) * mm});
            skLineSegment(sketch, "E83.9.0.1", {"start": v(0, -1828.8) * mm, "end": v(0, 1828.8) * mm});
            skLineSegment(sketch, "E83.10.0.0", {"start": v(-444.5, -1828.8) * mm, "end": v(-444.5, 1828.8) * mm});
            skLineSegment(sketch, "E83.10.0.1", {"start": v(-406.4, -1828.8) * mm, "end": v(-406.4, 1828.8) * mm});
            skLineSegment(sketch, "E83.11.0.0", {"start": v(-850.9, -1828.8) * mm, "end": v(-850.9, 1828.8) * mm});
            skLineSegment(sketch, "E83.11.0.1", {"start": v(-812.8, -1828.8) * mm, "end": v(-812.8, 1828.8) * mm});
            skLineSegment(sketch, "E83.12.0.0", {"start": v(-1257.3, -1828.8) * mm, "end": v(-1257.3, 1828.8) * mm});
            skLineSegment(sketch, "E83.12.0.1", {"start": v(-1219.2, -1828.8) * mm, "end": v(-1219.2, 1828.8) * mm});
            skLineSegment(sketch, "E83.13.0.0", {"start": v(-1663.7, -1828.8) * mm, "end": v(-1663.7, 1828.8) * mm});
            skLineSegment(sketch, "E83.13.0.1", {"start": v(-1625.6, -1828.8) * mm, "end": v(-1625.6, 1828.8) * mm});
            skLineSegment(sketch, "E83.14.0.0", {"start": v(-2070.1, -1828.8) * mm, "end": v(-2070.1, 1828.8) * mm});
            skLineSegment(sketch, "E83.14.0.1", {"start": v(-2032, -1828.8) * mm, "end": v(-2032, 1828.8) * mm});
            skLineSegment(sketch, "E83.15.0.0", {"start": v(-2476.5, -1828.8) * mm, "end": v(-2476.5, 1828.8) * mm});
            skLineSegment(sketch, "E83.15.0.1", {"start": v(-2438.4, -1828.8) * mm, "end": v(-2438.4, 1828.8) * mm});
            skLineSegment(sketch, "E83.16.0.0", {"start": v(-2882.9, -1828.8) * mm, "end": v(-2882.9, 1828.8) * mm});
            skLineSegment(sketch, "E83.16.0.1", {"start": v(-2844.8, -1828.8) * mm, "end": v(-2844.8, 1828.8) * mm});
            skLineSegment(sketch, "E83.17.0.0", {"start": v(-3289.3, -1828.8) * mm, "end": v(-3289.3, 1828.8) * mm});
            skLineSegment(sketch, "E83.17.0.1", {"start": v(-3251.2, -1828.8) * mm, "end": v(-3251.2, 1828.8) * mm});
            skLineSegment(sketch, "E83.direction1", {"start": v(3619.5, -1828.8) * mm, "end": v(3213.1, -1828.8) * mm, "construction": true});
            skLineSegment(sketch, "E84", {"start": v(3657.6, 101.6) * mm, "end": v(-3657.6, 101.6) * mm});
            skLineSegment(sketch, "E85", {"start": v(-3657.6, -101.6) * mm, "end": v(3657.6, -101.6) * mm});
            skLineSegment(sketch, "E86", {"start": v(-3657.6, 0) * mm, "end": v(3657.6, 0) * mm, "construction": true});
            skLineSegment(sketch, "E87", {"start": v(3657.6, -1625.6) * mm, "end": v(-3657.6, -1625.6) * mm});
            skLineSegment(sketch, "E88", {"start": v(3657.6, 1625.6) * mm, "end": v(-3657.6, 1625.6) * mm});
            skLineSegment(sketch, "E89", {"start": v(88.9, -1739.9) * mm, "end": v(3568.7, 1739.9) * mm, "construction": true});
            skLineSegment(sketch, "E90", {"start": v(3568.7, -1739.9) * mm, "end": v(88.9, 1739.9) * mm, "construction": true});
            skCircle(sketch, "E91", {"center": v(1828.8, 0) * mm, "radius": 50.8 * mm});
            skCircle(sketch, "E92", {"center": v(2014.37, -734.82) * mm, "radius": 292.1 * mm});
            skLineSegment(sketch, "E93", {"start": v(1828.8, 0) * mm, "end": v(1955.69, -564.5) * mm});
            skSolve(sketch);
        }
        {
            var Q0;
            Q0=makeQuery(id+"F11.opExtrude","SWEPT_FACE",FACE,{"disambiguationData":[OSD([sQuery(id+"F10.wireOp",EDGE,"E14")])]});
            var sketch = newSketch(context, id + "F61", { "sketchPlane" : qUnion([Q0])});
            skLineSegment(sketch, "E94.bottom", {"start": v(1739.9, 152.4) * mm, "end": v(927.1, 152.4) * mm});
            skLineSegment(sketch, "E94.top", {"start": v(1739.9, 1371.6) * mm, "end": v(927.1, 1371.6) * mm});
            skLineSegment(sketch, "E94.left", {"start": v(1739.9, 152.4) * mm, "end": v(1739.9, 1371.6) * mm});
            skLineSegment(sketch, "E94.right", {"start": v(927.1, 152.4) * mm, "end": v(927.1, 1371.6) * mm});
            skSolve(sketch);
        }
        {
            var Q0;
            Q0=qSketchRegion(id+"F61",true);
            extrude(context, id + "F62", {"entities" : qUnion([Q0]), "operationType" : NewBodyOperationType.REMOVE, "oppositeDirection" : true, "depth" : 12.7 * mm, "offsetDistance" : 25.4 * mm});
        }
        {
            var Q0;
            Q0=makeQuery(id+"F62.boolean.opBoolean","COPY",FACE,{"derivedFrom":makeQuery(id+"F62.opExtrude","CAP_FACE",FACE,{"disambiguationData":[OSD([sQuery(id+"F61.wireOp",EDGE,"E94.bottom"),sQuery(id+"F61.wireOp",EDGE,"E94.top"),sQuery(id+"F61.wireOp",EDGE,"E94.left"),sQuery(id+"F61.wireOp",EDGE,"E94.right")])],"isStart":false})});
            var sketch = newSketch(context, id + "F63", { "sketchPlane" : qUnion([Q0])});
            skLineSegment(sketch, "E95.bottom", {"start": v(1530.35, 152.4) * mm, "end": v(1136.65, 152.4) * mm});
            skLineSegment(sketch, "E95.top", {"start": v(1530.35, 660.4) * mm, "end": v(1136.65, 660.4) * mm});
            skLineSegment(sketch, "E95.left", {"start": v(1530.35, 152.4) * mm, "end": v(1530.35, 660.4) * mm});
            skLineSegment(sketch, "E95.right", {"start": v(1136.65, 152.4) * mm, "end": v(1136.65, 660.4) * mm});
            skSolve(sketch);
        }
        {
            var Q0;
            Q0=qSketchRegion(id+"F63",true);
            extrude(context, id + "F64", {"entities" : qUnion([Q0]), "operationType" : NewBodyOperationType.REMOVE, "endBound" : BoundingType.UP_TO_NEXT, "oppositeDirection" : true, "depth" : 25.4 * mm, "offsetDistance" : 25.4 * mm, "hasSecondDirection" : true, "secondDirectionBound" : SecondDirectionBoundingType.UP_TO_NEXT, "secondDirectionOppositeDirection" : false, "secondDirectionDepth" : 25.4 * mm});
        }
        {
            var Q0;
            Q0=makeQuery(id+"F1.opExtrude","CAP_FACE",FACE,{"disambiguationData":[OSD([sQuery(id+"F0.wireOp",EDGE,"E0.bottom"),sQuery(id+"F0.wireOp",EDGE,"E0.top"),sQuery(id+"F0.wireOp",EDGE,"E0.left"),sQuery(id+"F0.wireOp",EDGE,"E0.right")])],"isStart":false});
            var sketch = newSketch(context, id + "F65", { "sketchPlane" : qUnion([Q0])});
            skLineSegment(sketch, "E96", {"start": v(-2781.3, -1828.8) * mm, "end": v(-2746.77, -1812.7) * mm});
            skLineSegment(sketch, "E97", {"start": v(-2746.77, -1812.7) * mm, "end": v(-2360.25, -2641.39) * mm});
            skLineSegment(sketch, "E98", {"start": v(-2360.25, -2641.39) * mm, "end": v(-2394.78, -2657.5) * mm});
            skLineSegment(sketch, "E99", {"start": v(-2394.78, -2657.5) * mm, "end": v(-2781.3, -1828.8) * mm});
            skLineSegment(sketch, "E100", {"start": v(-952.5, -1828.8) * mm, "end": v(-987.03, -1812.7) * mm});
            skLineSegment(sketch, "E101", {"start": v(-987.03, -1812.7) * mm, "end": v(-1373.55, -2641.39) * mm});
            skLineSegment(sketch, "E102", {"start": v(-1373.55, -2641.39) * mm, "end": v(-1339.02, -2657.5) * mm});
            skLineSegment(sketch, "E103", {"start": v(-1339.02, -2657.5) * mm, "end": v(-952.5, -1828.8) * mm});
            skSolve(sketch);
        }
        {
            var Q0;
            Q0=qSketchRegion(id+"F65",true);
            extrude(context, id + "F66", {"entities" : qUnion([Q0]), "depth" : 2082.8 * mm, "offsetDistance" : 25.4 * mm});
        }
        {
            var Q0;
            Q0=makeQuery(id+"F27.opExtrude","CAP_EDGE",EDGE,{"disambiguationData":[OSD([sQuery(id+"F26.wireOp",EDGE,"E26.right")])],"isStart":false});
            var Q1;
            Q1=makeQuery(id+"F43.boolean.opBoolean","COPY",EDGE,{"derivedFrom":makeQuery(id+"F43.opExtrude","SWEPT_EDGE",EDGE,{"disambiguationData":[OSD([sQuery(id+"F40.wireOp",EDGE,"E45.bottom"),sQuery(id+"F42.wireOp",EDGE,"E47"),sQuery(id+"F42.wireOp",EDGE,"E48")])]})});
            var Q2;
            Q2=makeQuery(id+"F43.boolean.opBoolean","COPY",EDGE,{"derivedFrom":makeQuery(id+"F43.opExtrude","SWEPT_EDGE",EDGE,{"disambiguationData":[OSD([sQuery(id+"F40.wireOp",EDGE,"E45.bottom"),sQuery(id+"F40.wireOp",EDGE,"E45.right"),sQuery(id+"F42.wireOp",EDGE,"E46"),sQuery(id+"F42.wireOp",EDGE,"E47")])]})});
            fillet(context, id + "F67", {"entities" : qUnion([Q0, Q1, Q2]), "radius" : 50.8 * mm, "tangentPropagation" : true, "allowEdgeOverflow" : false});
        }
        {
            var Q0;
            Q0=makeQuery(id+"F3.opExtrude","SWEPT_FACE",FACE,{"disambiguationData":[OSD([sQuery(id+"F2.wireOp",EDGE,"E2.bottom")])]});
            var sketch = newSketch(context, id + "F68", { "sketchPlane" : qUnion([Q0])});
            skLineSegment(sketch, "E104.bottom", {"start": v(584.2, 203.2) * mm, "end": v(1193.8, 203.2) * mm});
            skLineSegment(sketch, "E104.top", {"start": v(584.2, 1346.2) * mm, "end": v(1193.8, 1346.2) * mm});
            skLineSegment(sketch, "E104.left", {"start": v(584.2, 203.2) * mm, "end": v(584.2, 1346.2) * mm});
            skLineSegment(sketch, "E104.right", {"start": v(1193.8, 203.2) * mm, "end": v(1193.8, 1346.2) * mm});
            skSolve(sketch);
        }
        {
            var Q0;
            Q0 = qSketchRegion(id + "F68", true);
            extrude(context, id + "F69", {"entities" : qUnion([Q0]), "operationType" : NewBodyOperationType.ADD, "depth" : 88.9 * mm, "offsetDistance" : 25.4 * mm});
        }
        {
            var Q0;
            Q0=makeQuery(id+"F11.opExtrude","SWEPT_FACE",FACE,{"disambiguationData":[OSD([sQuery(id+"F10.wireOp",EDGE,"E11")])]});
            var sketch = newSketch(context, id + "F70", { "sketchPlane" : qUnion([Q0])});
            skLineSegment(sketch, "E105.bottom", {"start": v(-927.1, 203.2) * mm, "end": v(-1651, 203.2) * mm});
            skLineSegment(sketch, "E105.top", {"start": v(-927.1, 1346.2) * mm, "end": v(-1651, 1346.2) * mm});
            skLineSegment(sketch, "E105.left", {"start": v(-927.1, 203.2) * mm, "end": v(-927.1, 1346.2) * mm});
            skLineSegment(sketch, "E105.right", {"start": v(-1651, 203.2) * mm, "end": v(-1651, 1346.2) * mm});
            skSolve(sketch);
        }
        {
            var Q0;
            Q0 = qSketchRegion(id + "F70", true);
            extrude(context, id + "F71", {"entities" : qUnion([Q0]), "operationType" : NewBodyOperationType.REMOVE, "oppositeDirection" : true, "depth" : 12.7 * mm, "offsetDistance" : 25.4 * mm});
        }
    });
